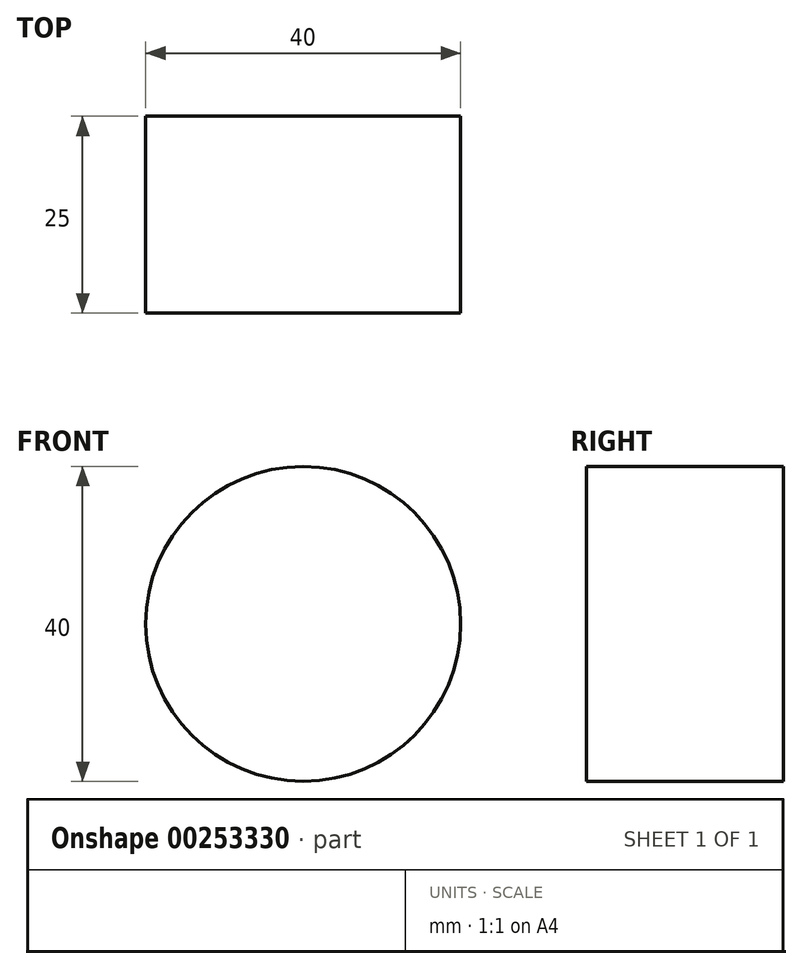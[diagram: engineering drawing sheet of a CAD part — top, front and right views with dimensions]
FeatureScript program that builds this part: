
annotation { "Feature Type Name" : "Feature", "Feature Type Description" : "" }
export const myFeature = defineFeature(function(context is Context, id is Id, definition is map)
    precondition{}
    {
        {
            var Q0;
            Q0=qCreatedBy(makeId("Front.planeOp"),FACE);
            var sketch = newSketch(context, id + "F0", { "sketchPlane" : qUnion([Q0])});
            skCircle(sketch, "E0", {"center": v(0, 0) * mm, "radius": 20 * mm});
            skSolve(sketch);
        }
        {
            var Q0;
            Q0 = qSketchRegion(id + "F0", true);
            extrude(context, id + "F1", {"entities" : qUnion([Q0]), "depth" : 25 * mm});
        }
    });
